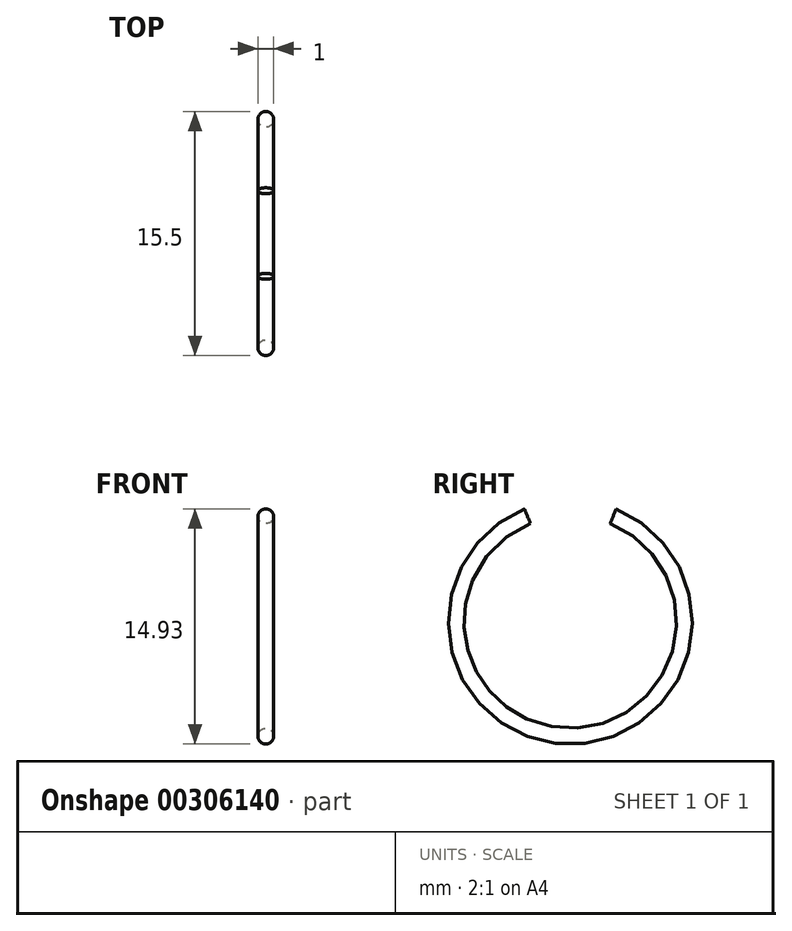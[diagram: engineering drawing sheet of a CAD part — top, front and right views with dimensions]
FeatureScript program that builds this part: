
annotation { "Feature Type Name" : "Feature", "Feature Type Description" : "" }
export const myFeature = defineFeature(function(context is Context, id is Id, definition is map)
    precondition{}
    {
        {
            var Q0;
            Q0=qCreatedBy(makeId("Front.planeOp"),FACE);
            var sketch = newSketch(context, id + "F0", { "sketchPlane" : qUnion([Q0])});
            skPoint(sketch, "E0", {"position": v(0, 0) * mm});
            skPoint(sketch, "E1", {"position": v(0, 7.25) * mm});
            skCircle(sketch, "E2", {"center": v(0, 7.25) * mm, "radius": 0.5 * mm});
            skLineSegment(sketch, "E3", {"start": v(-9.62, 0) * mm, "end": v(8.02, 0) * mm});
            skSolve(sketch);
        }
        {
            var Q0;
            Q0=makeQuery(id+"F0.imprint","IMPRINT",FACE,{"disambiguationData":[TD([[makeQuery(id+"F0.imprint","IMPRINT",EDGE,{"derivedFrom":sQuery(id+"F0.wireOp",EDGE,"E2")}),1.0]])]});
            var Q1;
            Q1=sQuery(id+"F0.wireOp",EDGE,"E3");
            revolve(context, id + "F1", {"entities" : qUnion([Q0]), "axis" : qUnion([Q1]), "revolveType" : RevolveType.FULL});
        }
        {
            var Q0;
            Q0=qCreatedBy(makeId("Right.planeOp"),FACE);
            var sketch = newSketch(context, id + "F2", { "sketchPlane" : qUnion([Q0])});
            skLineSegment(sketch, "E4", {"start": v(0, 0) * mm, "end": v(-7.5, 18.54) * mm});
            skLineSegment(sketch, "E5", {"start": v(0, 0) * mm, "end": v(7.5, 18.54) * mm});
            skLineSegment(sketch, "E6", {"start": v(7.5, 18.54) * mm, "end": v(-7.5, 18.54) * mm});
            skSolve(sketch);
        }
        {
            var Q0;
            Q0=makeQuery(id+"F2.imprint","IMPRINT",FACE,{"disambiguationData":[TD([[makeQuery(id+"F2.imprint","IMPRINT",EDGE,{"derivedFrom":sQuery(id+"F2.wireOp",EDGE,"E4")}),-1.0]])]});
            extrude(context, id + "F3", {"entities" : qUnion([Q0]), "operationType" : NewBodyOperationType.REMOVE, "endBound" : BoundingType.SYMMETRIC, "oppositeDirection" : true, "depth" : 25 * mm});
        }
    });
